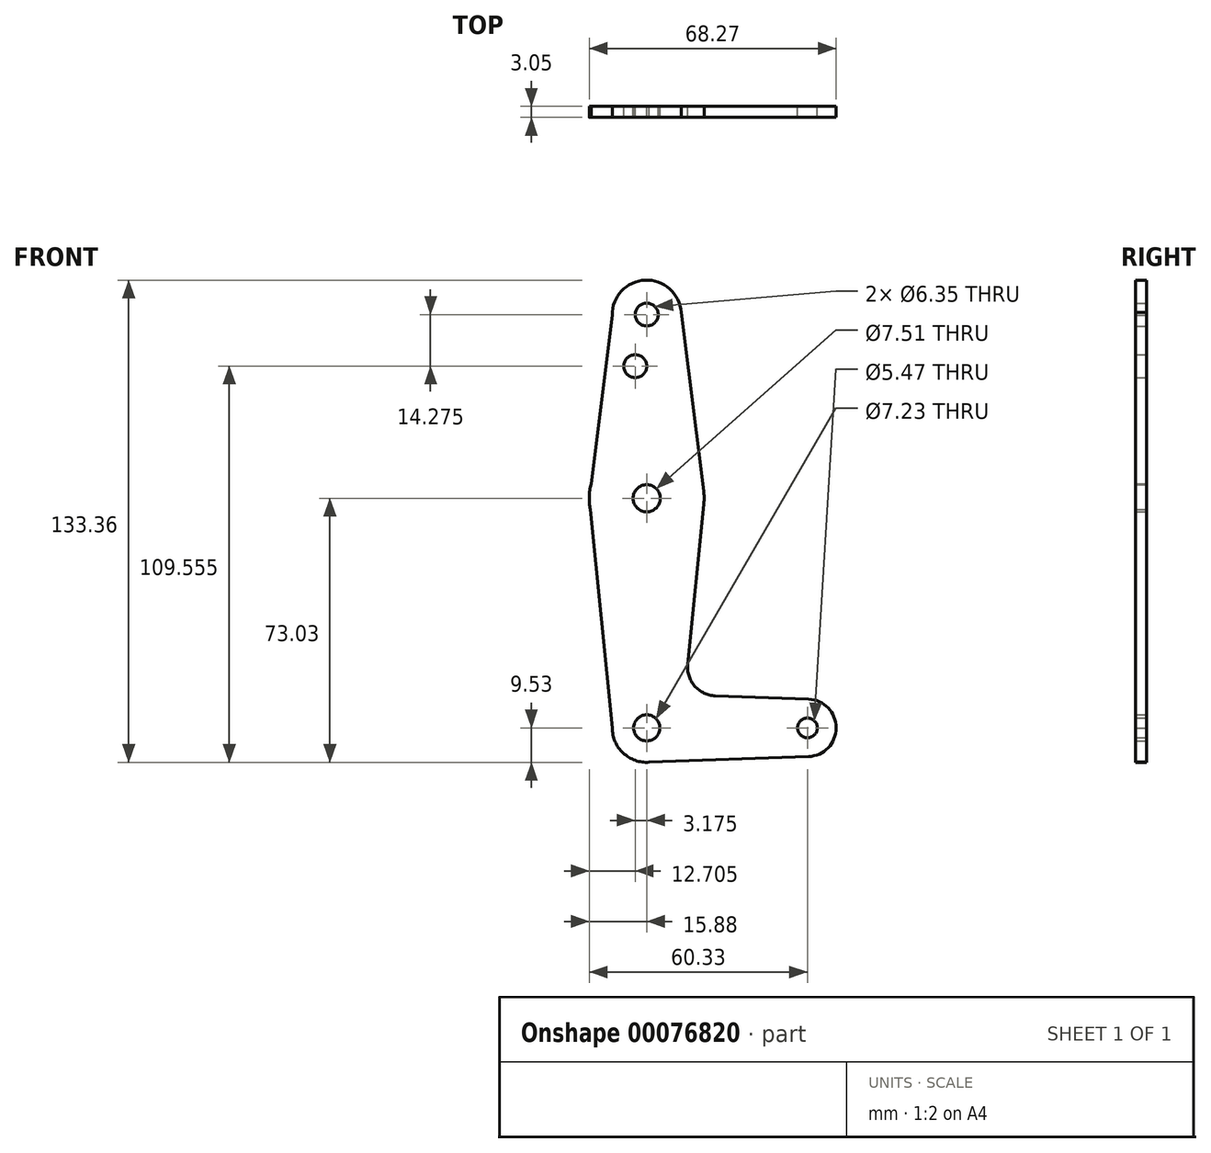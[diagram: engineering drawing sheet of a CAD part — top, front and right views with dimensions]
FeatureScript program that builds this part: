
annotation { "Feature Type Name" : "Feature", "Feature Type Description" : "" }
export const myFeature = defineFeature(function(context is Context, id is Id, definition is map)
    precondition{}
    {
        {
            var Q0;
            Q0=qCreatedBy(makeId("Front.planeOp"),FACE);
            var sketch = newSketch(context, id + "F0", { "sketchPlane" : qUnion([Q0])});
            skLineSegment(sketch, "E0", {"start": v(0, 0) * mm, "end": v(0, 114.3) * mm});
            skLineSegment(sketch, "E1", {"start": v(0, 0) * mm, "end": v(44.45, 0) * mm});
            skCircle(sketch, "E2", {"center": v(0, 114.3) * mm, "radius": 9.53 * mm});
            skCircle(sketch, "E3", {"center": v(0, 63.5) * mm, "radius": 15.88 * mm});
            skCircle(sketch, "E4", {"center": v(44.45, 0) * mm, "radius": 7.94 * mm});
            skCircle(sketch, "E5", {"center": v(0, 0) * mm, "radius": 9.53 * mm});
            skLineSegment(sketch, "E6", {"start": v(18.97, 8.85) * mm, "end": v(44.73, 7.93) * mm});
            skLineSegment(sketch, "E7", {"start": v(0, -9.53) * mm, "end": v(44.73, -7.93) * mm});
            skArc(sketch, "E8.filletArc", {"start": v(11.34, 17.59) * mm, "mid": v(13.26, 11.57) * mm, "end": v(18.97, 8.85) * mm});
            skLineSegment(sketch, "E9", {"start": v(9.5, 114.93) * mm, "end": v(15.75, 65.49) * mm});
            skCircle(sketch, "E10", {"center": v(-3.18, 100.03) * mm, "radius": 3.18 * mm});
            skCircle(sketch, "E11", {"center": v(0, 114.3) * mm, "radius": 3.18 * mm});
            skCircle(sketch, "E12", {"center": v(0, 63.5) * mm, "radius": 3.76 * mm});
            skCircle(sketch, "E13", {"center": v(0, 0) * mm, "radius": 3.61 * mm});
            skCircle(sketch, "E14", {"center": v(44.45, 0) * mm, "radius": 2.73 * mm});
            skLineSegment(sketch, "E15", {"start": v(15.8, 61.98) * mm, "end": v(11.34, 17.59) * mm});
            skLineSegment(sketch, "E16", {"start": v(-9.52, 114.08) * mm, "end": v(-15.87, 63.44) * mm});
            skLineSegment(sketch, "E17", {"start": v(-9.52, 0) * mm, "end": v(-15.87, 63.44) * mm});
            skSolve(sketch);
        }
        {
            var Q0;
            Q0 = qSketchRegion(id + "F0", true);
            var Q1;
            {var subQ0=sQuery(id+"F0.wireOp",EDGE,"E13");var subQ1=sQuery(id+"F0.wireOp",EDGE,"E0");var subQ2=makeQuery(id+"F0.imprint","INTERSECT",VERTEX,{"derivedFrom":[subQ1,subQ0]});Q1=makeQuery(id+"F0.imprint","IMPRINT",FACE,{"disambiguationData":[TD([[makeQuery(id+"F0.imprint","IMPRINT",EDGE,{"disambiguationData":[TD([[subQ2,-1.0]])],"derivedFrom":subQ1}),-1.0]])]});}
            extrude(context, id + "F1", {"entities" : qUnion([Q0, Q1]), "depth" : 3.05 * mm});
        }
    });
